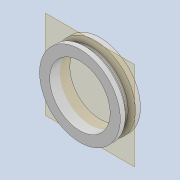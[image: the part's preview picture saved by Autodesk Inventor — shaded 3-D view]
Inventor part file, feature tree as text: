
AUTODESK INVENTOR PART (.ipt)
format: ipt  version: 2020 (Build 240168000, 168)  size: 124,416 bytes
history: native  units: mm
features: other x3, sketch x2, extrude x1, plane x1, revolve x1, fillet x1, reference x1
ambient origin geometry x8: Origin, YZ Plane, XZ Plane, XY Plane, X Axis, Y Axis, Z Axis, Center Point
bodies: Solid1 (feature_tree)
feature tree (10):
  extrude  "Extrusion1"  Depth=8.0mm
  plane  "Work Plane1"
  revolve  "Revolution1"  [1 undecoded]
  fillet  "Fillet1"  Radius=0.5mm
  sketch  "Sketch1"  dims[d0=6.0mm d1=8.0mm]
  reference  "Reference1"
  sketch  "Sketch2"  dims[d2=2.0mm d3=0.0mm d4=0.5mm d5=0.5mm d6=0.5mm d7=90.0deg d8=0.2mm]
  parser-record x1  (decoder bookkeeping rows leaked as tree rows — omitted from the tree; the rows remain in map.json)
  other  "tip_3_ass.iam"
  other  "bearing_3_6_2:4"
note: 1 file-system path scrubbed to <path> (originals preserved in map.json)
note: 1 required parameter value undecoded (feature->parameter linkage not recoverable at this tier; creation-order binding heuristic only, values carry confidence <= 0.55)
